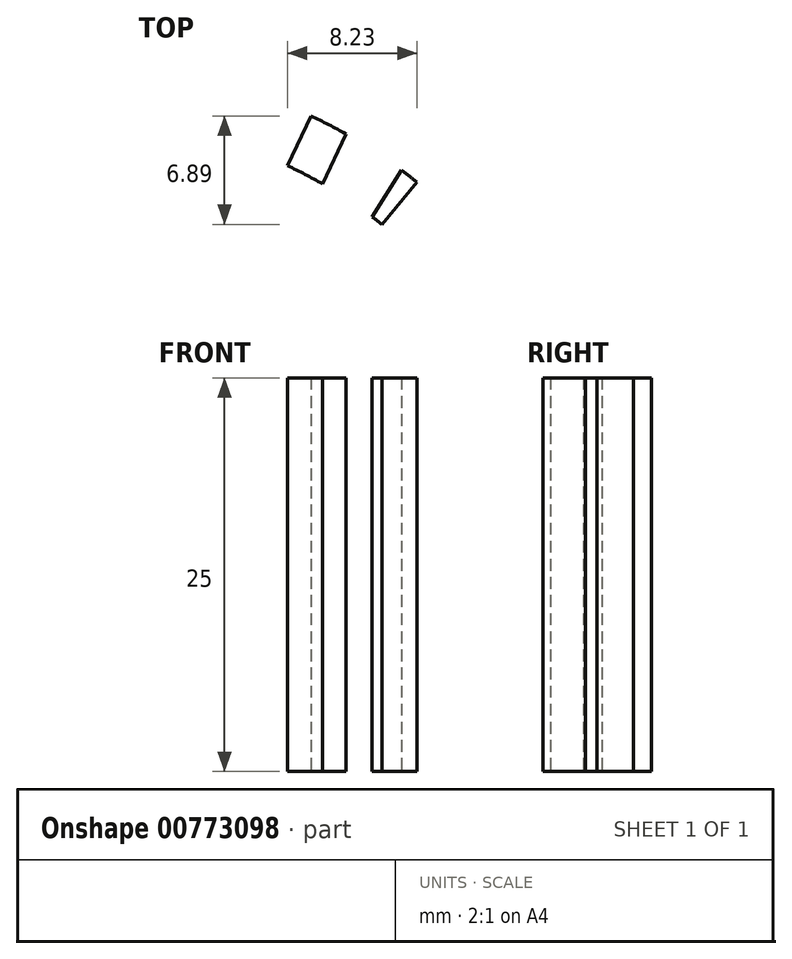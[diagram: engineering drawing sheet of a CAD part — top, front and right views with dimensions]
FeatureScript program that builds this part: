
annotation { "Feature Type Name" : "Feature", "Feature Type Description" : "" }
export const myFeature = defineFeature(function(context is Context, id is Id, definition is map)
    precondition{}
    {
        {
            var Q0;
            Q0=qCreatedBy(makeId("Top.planeOp"),FACE);
            var sketch = newSketch(context, id + "F0", { "sketchPlane" : qUnion([Q0])});
            skCircle(sketch, "E0", {"center": v(0, 0) * mm, "radius": 33.66 * mm});
            skCircle(sketch, "E1", {"center": v(0, 0) * mm, "radius": 30.16 * mm});
            skLineSegment(sketch, "E2", {"start": v(33.66, 0) * mm, "end": v(30.16, 0) * mm});
            skLineSegment(sketch, "E3", {"start": v(33.6, -2) * mm, "end": v(30.1, -2) * mm});
            skLineSegment(sketch, "E4", {"start": v(30.16, 0.5) * mm, "end": v(33.65, 0.5) * mm});
            skLineSegment(sketch, "E5", {"start": v(33.65, 0.5) * mm, "end": v(33.65, 0.5) * mm});
            skLineSegment(sketch, "E6", {"start": v(33.56, -2.5) * mm, "end": v(30.06, -2.5) * mm});
            skLineSegment(sketch, "E7.1.0", {"start": v(33.61, 1.73) * mm, "end": v(30.14, 1.29) * mm});
            skLineSegment(sketch, "E7.1.1", {"start": v(33.58, 2.23) * mm, "end": v(30.11, 1.79) * mm});
            skLineSegment(sketch, "E7.1.2", {"start": v(29.86, 4.28) * mm, "end": v(33.32, 4.71) * mm});
            skLineSegment(sketch, "E7.1.3", {"start": v(33.4, 4.22) * mm, "end": v(29.93, 3.78) * mm});
            skLineSegment(sketch, "E7.2.0", {"start": v(33.13, 5.93) * mm, "end": v(29.74, 5.06) * mm});
            skLineSegment(sketch, "E7.2.1", {"start": v(33.04, 6.42) * mm, "end": v(29.65, 5.55) * mm});
            skLineSegment(sketch, "E7.2.2", {"start": v(29.09, 7.98) * mm, "end": v(32.47, 8.85) * mm});
            skLineSegment(sketch, "E7.2.3", {"start": v(32.6, 8.37) * mm, "end": v(29.22, 7.5) * mm});
            skLineSegment(sketch, "E7.3.0", {"start": v(32.13, 10.03) * mm, "end": v(28.87, 8.74) * mm});
            skLineSegment(sketch, "E7.3.1", {"start": v(31.97, 10.5) * mm, "end": v(28.72, 9.22) * mm});
            skLineSegment(sketch, "E7.3.2", {"start": v(27.86, 11.57) * mm, "end": v(31.1, 12.85) * mm});
            skLineSegment(sketch, "E7.3.3", {"start": v(31.3, 12.39) * mm, "end": v(28.05, 11.1) * mm});
            skLineSegment(sketch, "E7.4.0", {"start": v(30.62, 13.98) * mm, "end": v(27.55, 12.3) * mm});
            skLineSegment(sketch, "E7.4.1", {"start": v(30.4, 14.43) * mm, "end": v(27.34, 12.75) * mm});
            skLineSegment(sketch, "E7.4.2", {"start": v(26.19, 14.97) * mm, "end": v(29.25, 16.65) * mm});
            skLineSegment(sketch, "E7.4.3", {"start": v(29.5, 16.21) * mm, "end": v(26.43, 14.53) * mm});
            skLineSegment(sketch, "E7.5.0", {"start": v(28.62, 17.7) * mm, "end": v(25.79, 15.65) * mm});
            skLineSegment(sketch, "E7.5.1", {"start": v(28.36, 18.13) * mm, "end": v(25.53, 16.07) * mm});
            skLineSegment(sketch, "E7.5.2", {"start": v(24.1, 18.13) * mm, "end": v(26.93, 20.18) * mm});
            skLineSegment(sketch, "E7.5.3", {"start": v(27.23, 19.78) * mm, "end": v(24.4, 17.73) * mm});
            skLineSegment(sketch, "E7.6.0", {"start": v(26.18, 21.15) * mm, "end": v(23.62, 18.76) * mm});
            skLineSegment(sketch, "E7.6.1", {"start": v(25.86, 21.54) * mm, "end": v(23.3, 19.15) * mm});
            skLineSegment(sketch, "E7.6.2", {"start": v(21.64, 21.01) * mm, "end": v(24.19, 23.4) * mm});
            skLineSegment(sketch, "E7.6.3", {"start": v(24.53, 23.04) * mm, "end": v(21.99, 20.65) * mm});
            skLineSegment(sketch, "E7.7.0", {"start": v(23.32, 24.27) * mm, "end": v(21.09, 21.57) * mm});
            skLineSegment(sketch, "E7.7.1", {"start": v(22.96, 24.61) * mm, "end": v(20.73, 21.92) * mm});
            skLineSegment(sketch, "E7.7.2", {"start": v(18.84, 23.56) * mm, "end": v(21.07, 26.25) * mm});
            skLineSegment(sketch, "E7.7.3", {"start": v(21.45, 25.93) * mm, "end": v(19.23, 23.24) * mm});
            skLineSegment(sketch, "E7.8.0", {"start": v(20.1, 27) * mm, "end": v(18.22, 24.04) * mm});
            skLineSegment(sketch, "E7.8.1", {"start": v(19.7, 27.3) * mm, "end": v(17.82, 24.34) * mm});
            skLineSegment(sketch, "E7.8.2", {"start": v(15.74, 25.73) * mm, "end": v(17.6, 28.68) * mm});
            skLineSegment(sketch, "E7.8.3", {"start": v(18.03, 28.42) * mm, "end": v(16.16, 25.47) * mm});
            skLineSegment(sketch, "E7.9.0", {"start": v(16.55, 29.3) * mm, "end": v(15.06, 26.14) * mm});
            skLineSegment(sketch, "E7.9.1", {"start": v(16.11, 29.55) * mm, "end": v(14.62, 26.38) * mm});
            skLineSegment(sketch, "E7.9.2", {"start": v(12.39, 27.5) * mm, "end": v(13.88, 30.66) * mm});
            skLineSegment(sketch, "E7.9.3", {"start": v(14.33, 30.45) * mm, "end": v(12.84, 27.3) * mm});
            skLineSegment(sketch, "E7.10.0", {"start": v(12.75, 31.15) * mm, "end": v(11.67, 27.82) * mm});
            skLineSegment(sketch, "E7.10.1", {"start": v(12.28, 31.33) * mm, "end": v(11.2, 28) * mm});
            skLineSegment(sketch, "E7.10.2", {"start": v(8.84, 28.84) * mm, "end": v(9.92, 32.16) * mm});
            skLineSegment(sketch, "E7.10.3", {"start": v(10.4, 32) * mm, "end": v(9.32, 28.69) * mm});
            skLineSegment(sketch, "E7.11.0", {"start": v(8.74, 32.5) * mm, "end": v(8.09, 29.06) * mm});
            skLineSegment(sketch, "E7.11.1", {"start": v(8.26, 32.63) * mm, "end": v(7.6, 29.19) * mm});
            skLineSegment(sketch, "E7.11.2", {"start": v(5.16, 29.72) * mm, "end": v(5.81, 33.15) * mm});
            skLineSegment(sketch, "E7.11.3", {"start": v(6.3, 33.06) * mm, "end": v(5.65, 29.63) * mm});
            skLineSegment(sketch, "E7.12.0", {"start": v(4.6, 33.34) * mm, "end": v(4.38, 29.84) * mm});
            skLineSegment(sketch, "E7.12.1", {"start": v(4.1, 33.4) * mm, "end": v(3.89, 29.91) * mm});
            skLineSegment(sketch, "E7.12.2", {"start": v(1.4, 30.13) * mm, "end": v(1.61, 33.62) * mm});
            skLineSegment(sketch, "E7.12.3", {"start": v(2.11, 33.59) * mm, "end": v(1.9, 30.1) * mm});
            skLineSegment(sketch, "E7.13.0", {"start": v(0.39, 33.65) * mm, "end": v(0.6, 30.16) * mm});
            skLineSegment(sketch, "E7.13.1", {"start": v(-0.11, 33.66) * mm, "end": v(0.1, 30.16) * mm});
            skLineSegment(sketch, "E7.13.2", {"start": v(-2.4, 30.07) * mm, "end": v(-2.61, 33.55) * mm});
            skLineSegment(sketch, "E7.13.3", {"start": v(-2.11, 33.59) * mm, "end": v(-1.9, 30.1) * mm});
            skLineSegment(sketch, "E7.14.0", {"start": v(-3.83, 33.44) * mm, "end": v(-3.18, 30) * mm});
            skLineSegment(sketch, "E7.14.1", {"start": v(-4.33, 33.38) * mm, "end": v(-3.68, 29.94) * mm});
            skLineSegment(sketch, "E7.14.2", {"start": v(-6.14, 29.53) * mm, "end": v(-6.8, 32.96) * mm});
            skLineSegment(sketch, "E7.14.3", {"start": v(-6.3, 33.06) * mm, "end": v(-5.65, 29.63) * mm});
            skLineSegment(sketch, "E7.15.0", {"start": v(-8, 32.7) * mm, "end": v(-6.91, 29.36) * mm});
            skLineSegment(sketch, "E7.15.1", {"start": v(-8.48, 32.57) * mm, "end": v(-7.4, 29.24) * mm});
            skLineSegment(sketch, "E7.15.2", {"start": v(-9.8, 28.53) * mm, "end": v(-10.87, 31.85) * mm});
            skLineSegment(sketch, "E7.15.3", {"start": v(-10.4, 32) * mm, "end": v(-9.32, 28.69) * mm});
            skLineSegment(sketch, "E7.16.0", {"start": v(-12.03, 31.43) * mm, "end": v(-10.54, 28.26) * mm});
            skLineSegment(sketch, "E7.16.1", {"start": v(-12.5, 31.25) * mm, "end": v(-11, 28.08) * mm});
            skLineSegment(sketch, "E7.16.2", {"start": v(-13.3, 27.08) * mm, "end": v(-14.78, 30.24) * mm});
            skLineSegment(sketch, "E7.16.3", {"start": v(-14.33, 30.45) * mm, "end": v(-12.84, 27.3) * mm});
            skLineSegment(sketch, "E7.17.0", {"start": v(-15.87, 29.68) * mm, "end": v(-14, 26.72) * mm});
            skLineSegment(sketch, "E7.17.1", {"start": v(-16.31, 29.44) * mm, "end": v(-14.44, 26.48) * mm});
            skLineSegment(sketch, "E7.17.2", {"start": v(-16.58, 25.2) * mm, "end": v(-18.45, 28.15) * mm});
            skLineSegment(sketch, "E7.17.3", {"start": v(-18.03, 28.42) * mm, "end": v(-16.16, 25.47) * mm});
            skLineSegment(sketch, "E7.18.0", {"start": v(-19.47, 27.45) * mm, "end": v(-17.24, 24.75) * mm});
            skLineSegment(sketch, "E7.18.1", {"start": v(-19.87, 27.16) * mm, "end": v(-17.64, 24.47) * mm});
            skLineSegment(sketch, "E7.18.2", {"start": v(-19.6, 22.92) * mm, "end": v(-21.84, 25.61) * mm});
            skLineSegment(sketch, "E7.18.3", {"start": v(-21.45, 25.93) * mm, "end": v(-19.23, 23.24) * mm});
            skLineSegment(sketch, "E7.19.0", {"start": v(-22.76, 24.8) * mm, "end": v(-20.2, 22.4) * mm});
            skLineSegment(sketch, "E7.19.1", {"start": v(-23.12, 24.46) * mm, "end": v(-20.57, 22.06) * mm});
            skLineSegment(sketch, "E7.19.2", {"start": v(-22.33, 20.28) * mm, "end": v(-24.87, 22.67) * mm});
            skLineSegment(sketch, "E7.19.3", {"start": v(-24.53, 23.04) * mm, "end": v(-21.99, 20.65) * mm});
            skLineSegment(sketch, "E7.20.0", {"start": v(-25.68, 21.75) * mm, "end": v(-22.85, 19.7) * mm});
            skLineSegment(sketch, "E7.20.1", {"start": v(-26, 21.37) * mm, "end": v(-23.17, 19.3) * mm});
            skLineSegment(sketch, "E7.20.2", {"start": v(-24.7, 17.32) * mm, "end": v(-27.52, 19.38) * mm});
            skLineSegment(sketch, "E7.20.3", {"start": v(-27.23, 19.78) * mm, "end": v(-24.4, 17.73) * mm});
            skLineSegment(sketch, "E7.21.0", {"start": v(-28.2, 18.36) * mm, "end": v(-25.14, 16.67) * mm});
            skLineSegment(sketch, "E7.21.1", {"start": v(-28.48, 17.94) * mm, "end": v(-25.41, 16.25) * mm});
            skLineSegment(sketch, "E7.21.2", {"start": v(-26.67, 14.1) * mm, "end": v(-29.73, 15.77) * mm});
            skLineSegment(sketch, "E7.21.3", {"start": v(-29.5, 16.21) * mm, "end": v(-26.43, 14.53) * mm});
            skLineSegment(sketch, "E7.22.0", {"start": v(-30.29, 14.68) * mm, "end": v(-27.03, 13.39) * mm});
            skLineSegment(sketch, "E7.22.1", {"start": v(-30.5, 14.23) * mm, "end": v(-27.25, 12.94) * mm});
            skLineSegment(sketch, "E7.22.2", {"start": v(-28.23, 10.64) * mm, "end": v(-31.47, 11.92) * mm});
            skLineSegment(sketch, "E7.22.3", {"start": v(-31.3, 12.39) * mm, "end": v(-28.05, 11.1) * mm});
            skLineSegment(sketch, "E7.23.0", {"start": v(-31.89, 10.77) * mm, "end": v(-28.5, 9.9) * mm});
            skLineSegment(sketch, "E7.23.1", {"start": v(-32.04, 10.3) * mm, "end": v(-28.65, 9.42) * mm});
            skLineSegment(sketch, "E7.23.2", {"start": v(-29.34, 7.02) * mm, "end": v(-32.72, 7.88) * mm});
            skLineSegment(sketch, "E7.23.3", {"start": v(-32.6, 8.37) * mm, "end": v(-29.22, 7.5) * mm});
            skLineSegment(sketch, "E7.24.0", {"start": v(-32.98, 6.69) * mm, "end": v(-29.51, 6.25) * mm});
            skLineSegment(sketch, "E7.24.1", {"start": v(-33.08, 6.2) * mm, "end": v(-29.6, 5.76) * mm});
            skLineSegment(sketch, "E7.24.2", {"start": v(-29.98, 3.28) * mm, "end": v(-33.45, 3.72) * mm});
            skLineSegment(sketch, "E7.24.3", {"start": v(-33.4, 4.22) * mm, "end": v(-29.93, 3.78) * mm});
            skLineSegment(sketch, "E7.25.0", {"start": v(-33.56, 2.5) * mm, "end": v(-30.06, 2.5) * mm});
            skLineSegment(sketch, "E7.25.1", {"start": v(-33.6, 2) * mm, "end": v(-30.1, 2) * mm});
            skLineSegment(sketch, "E7.25.2", {"start": v(-30.16, -0.5) * mm, "end": v(-33.65, -0.5) * mm});
            skLineSegment(sketch, "E7.25.3", {"start": v(-33.66, 0) * mm, "end": v(-30.16, 0) * mm});
            skLineSegment(sketch, "E7.26.0", {"start": v(-33.61, -1.73) * mm, "end": v(-30.14, -1.29) * mm});
            skLineSegment(sketch, "E7.26.1", {"start": v(-33.58, -2.23) * mm, "end": v(-30.11, -1.79) * mm});
            skLineSegment(sketch, "E7.26.2", {"start": v(-29.86, -4.28) * mm, "end": v(-33.32, -4.71) * mm});
            skLineSegment(sketch, "E7.26.3", {"start": v(-33.4, -4.22) * mm, "end": v(-29.93, -3.78) * mm});
            skLineSegment(sketch, "E7.27.0", {"start": v(-33.13, -5.93) * mm, "end": v(-29.74, -5.06) * mm});
            skLineSegment(sketch, "E7.27.1", {"start": v(-33.04, -6.42) * mm, "end": v(-29.65, -5.55) * mm});
            skLineSegment(sketch, "E7.27.2", {"start": v(-29.09, -7.98) * mm, "end": v(-32.47, -8.85) * mm});
            skLineSegment(sketch, "E7.27.3", {"start": v(-32.6, -8.37) * mm, "end": v(-29.22, -7.5) * mm});
            skLineSegment(sketch, "E7.28.0", {"start": v(-32.13, -10.03) * mm, "end": v(-28.87, -8.74) * mm});
            skLineSegment(sketch, "E7.28.1", {"start": v(-31.97, -10.5) * mm, "end": v(-28.72, -9.22) * mm});
            skLineSegment(sketch, "E7.28.2", {"start": v(-27.86, -11.57) * mm, "end": v(-31.1, -12.85) * mm});
            skLineSegment(sketch, "E7.28.3", {"start": v(-31.3, -12.39) * mm, "end": v(-28.05, -11.1) * mm});
            skLineSegment(sketch, "E7.29.0", {"start": v(-30.62, -13.98) * mm, "end": v(-27.55, -12.3) * mm});
            skLineSegment(sketch, "E7.29.1", {"start": v(-30.4, -14.43) * mm, "end": v(-27.34, -12.75) * mm});
            skLineSegment(sketch, "E7.29.2", {"start": v(-26.19, -14.97) * mm, "end": v(-29.25, -16.65) * mm});
            skLineSegment(sketch, "E7.29.3", {"start": v(-29.5, -16.21) * mm, "end": v(-26.43, -14.53) * mm});
            skLineSegment(sketch, "E7.30.0", {"start": v(-28.62, -17.7) * mm, "end": v(-25.79, -15.65) * mm});
            skLineSegment(sketch, "E7.30.1", {"start": v(-28.36, -18.13) * mm, "end": v(-25.53, -16.07) * mm});
            skLineSegment(sketch, "E7.30.2", {"start": v(-24.1, -18.13) * mm, "end": v(-26.93, -20.18) * mm});
            skLineSegment(sketch, "E7.30.3", {"start": v(-27.23, -19.78) * mm, "end": v(-24.4, -17.73) * mm});
            skLineSegment(sketch, "E7.31.0", {"start": v(-26.18, -21.15) * mm, "end": v(-23.62, -18.76) * mm});
            skLineSegment(sketch, "E7.31.1", {"start": v(-25.86, -21.54) * mm, "end": v(-23.3, -19.15) * mm});
            skLineSegment(sketch, "E7.31.2", {"start": v(-21.64, -21.01) * mm, "end": v(-24.19, -23.4) * mm});
            skLineSegment(sketch, "E7.31.3", {"start": v(-24.53, -23.04) * mm, "end": v(-21.99, -20.65) * mm});
            skLineSegment(sketch, "E7.32.0", {"start": v(-23.32, -24.27) * mm, "end": v(-21.09, -21.57) * mm});
            skLineSegment(sketch, "E7.32.1", {"start": v(-22.96, -24.61) * mm, "end": v(-20.73, -21.92) * mm});
            skLineSegment(sketch, "E7.32.2", {"start": v(-18.84, -23.56) * mm, "end": v(-21.07, -26.25) * mm});
            skLineSegment(sketch, "E7.32.3", {"start": v(-21.45, -25.93) * mm, "end": v(-19.23, -23.24) * mm});
            skLineSegment(sketch, "E7.33.0", {"start": v(-20.1, -27) * mm, "end": v(-18.22, -24.04) * mm});
            skLineSegment(sketch, "E7.33.1", {"start": v(-19.7, -27.3) * mm, "end": v(-17.82, -24.34) * mm});
            skLineSegment(sketch, "E7.33.2", {"start": v(-15.74, -25.73) * mm, "end": v(-17.6, -28.68) * mm});
            skLineSegment(sketch, "E7.33.3", {"start": v(-18.03, -28.42) * mm, "end": v(-16.16, -25.47) * mm});
            skLineSegment(sketch, "E7.34.0", {"start": v(-16.55, -29.3) * mm, "end": v(-15.06, -26.14) * mm});
            skLineSegment(sketch, "E7.34.1", {"start": v(-16.11, -29.55) * mm, "end": v(-14.62, -26.38) * mm});
            skLineSegment(sketch, "E7.34.2", {"start": v(-12.39, -27.5) * mm, "end": v(-13.88, -30.66) * mm});
            skLineSegment(sketch, "E7.34.3", {"start": v(-14.33, -30.45) * mm, "end": v(-12.84, -27.3) * mm});
            skLineSegment(sketch, "E7.35.0", {"start": v(-12.75, -31.15) * mm, "end": v(-11.67, -27.82) * mm});
            skLineSegment(sketch, "E7.35.1", {"start": v(-12.28, -31.33) * mm, "end": v(-11.2, -28) * mm});
            skLineSegment(sketch, "E7.35.2", {"start": v(-8.84, -28.84) * mm, "end": v(-9.92, -32.16) * mm});
            skLineSegment(sketch, "E7.35.3", {"start": v(-10.4, -32) * mm, "end": v(-9.32, -28.69) * mm});
            skLineSegment(sketch, "E7.36.0", {"start": v(-8.74, -32.5) * mm, "end": v(-8.09, -29.06) * mm});
            skLineSegment(sketch, "E7.36.1", {"start": v(-8.26, -32.63) * mm, "end": v(-7.6, -29.19) * mm});
            skLineSegment(sketch, "E7.36.2", {"start": v(-5.16, -29.72) * mm, "end": v(-5.81, -33.15) * mm});
            skLineSegment(sketch, "E7.36.3", {"start": v(-6.3, -33.06) * mm, "end": v(-5.65, -29.63) * mm});
            skLineSegment(sketch, "E7.37.0", {"start": v(-4.6, -33.34) * mm, "end": v(-4.38, -29.84) * mm});
            skLineSegment(sketch, "E7.37.1", {"start": v(-4.1, -33.4) * mm, "end": v(-3.89, -29.91) * mm});
            skLineSegment(sketch, "E7.37.2", {"start": v(-1.4, -30.13) * mm, "end": v(-1.61, -33.62) * mm});
            skLineSegment(sketch, "E7.37.3", {"start": v(-2.11, -33.59) * mm, "end": v(-1.9, -30.1) * mm});
            skLineSegment(sketch, "E7.38.0", {"start": v(-0.39, -33.65) * mm, "end": v(-0.6, -30.16) * mm});
            skLineSegment(sketch, "E7.38.1", {"start": v(0.11, -33.66) * mm, "end": v(-0.1, -30.16) * mm});
            skLineSegment(sketch, "E7.38.2", {"start": v(2.4, -30.07) * mm, "end": v(2.61, -33.55) * mm});
            skLineSegment(sketch, "E7.38.3", {"start": v(2.11, -33.59) * mm, "end": v(1.9, -30.1) * mm});
            skLineSegment(sketch, "E7.39.0", {"start": v(3.83, -33.44) * mm, "end": v(3.18, -30) * mm});
            skLineSegment(sketch, "E7.39.1", {"start": v(4.33, -33.38) * mm, "end": v(3.68, -29.94) * mm});
            skLineSegment(sketch, "E7.39.2", {"start": v(6.14, -29.53) * mm, "end": v(6.8, -32.96) * mm});
            skLineSegment(sketch, "E7.39.3", {"start": v(6.3, -33.06) * mm, "end": v(5.65, -29.63) * mm});
            skLineSegment(sketch, "E7.40.0", {"start": v(8, -32.7) * mm, "end": v(6.91, -29.36) * mm});
            skLineSegment(sketch, "E7.40.1", {"start": v(8.48, -32.57) * mm, "end": v(7.4, -29.24) * mm});
            skLineSegment(sketch, "E7.40.2", {"start": v(9.8, -28.53) * mm, "end": v(10.87, -31.85) * mm});
            skLineSegment(sketch, "E7.40.3", {"start": v(10.4, -32) * mm, "end": v(9.32, -28.69) * mm});
            skLineSegment(sketch, "E7.41.0", {"start": v(12.03, -31.43) * mm, "end": v(10.54, -28.26) * mm});
            skLineSegment(sketch, "E7.41.1", {"start": v(12.5, -31.25) * mm, "end": v(11, -28.08) * mm});
            skLineSegment(sketch, "E7.41.2", {"start": v(13.3, -27.08) * mm, "end": v(14.78, -30.24) * mm});
            skLineSegment(sketch, "E7.41.3", {"start": v(14.33, -30.45) * mm, "end": v(12.84, -27.3) * mm});
            skLineSegment(sketch, "E7.42.0", {"start": v(15.87, -29.68) * mm, "end": v(14, -26.72) * mm});
            skLineSegment(sketch, "E7.42.1", {"start": v(16.31, -29.44) * mm, "end": v(14.44, -26.48) * mm});
            skLineSegment(sketch, "E7.42.2", {"start": v(16.58, -25.2) * mm, "end": v(18.45, -28.15) * mm});
            skLineSegment(sketch, "E7.42.3", {"start": v(18.03, -28.42) * mm, "end": v(16.16, -25.47) * mm});
            skLineSegment(sketch, "E7.43.0", {"start": v(19.47, -27.45) * mm, "end": v(17.24, -24.75) * mm});
            skLineSegment(sketch, "E7.43.1", {"start": v(19.87, -27.16) * mm, "end": v(17.64, -24.47) * mm});
            skLineSegment(sketch, "E7.43.2", {"start": v(19.6, -22.92) * mm, "end": v(21.84, -25.61) * mm});
            skLineSegment(sketch, "E7.43.3", {"start": v(21.45, -25.93) * mm, "end": v(19.23, -23.24) * mm});
            skLineSegment(sketch, "E7.44.0", {"start": v(22.76, -24.8) * mm, "end": v(20.2, -22.4) * mm});
            skLineSegment(sketch, "E7.44.1", {"start": v(23.12, -24.46) * mm, "end": v(20.57, -22.06) * mm});
            skLineSegment(sketch, "E7.44.2", {"start": v(22.33, -20.28) * mm, "end": v(24.87, -22.67) * mm});
            skLineSegment(sketch, "E7.44.3", {"start": v(24.53, -23.04) * mm, "end": v(21.99, -20.65) * mm});
            skLineSegment(sketch, "E7.45.0", {"start": v(25.68, -21.75) * mm, "end": v(22.85, -19.7) * mm});
            skLineSegment(sketch, "E7.45.1", {"start": v(26, -21.37) * mm, "end": v(23.17, -19.3) * mm});
            skLineSegment(sketch, "E7.45.2", {"start": v(24.7, -17.32) * mm, "end": v(27.52, -19.38) * mm});
            skLineSegment(sketch, "E7.45.3", {"start": v(27.23, -19.78) * mm, "end": v(24.4, -17.73) * mm});
            skLineSegment(sketch, "E7.46.0", {"start": v(28.2, -18.36) * mm, "end": v(25.14, -16.67) * mm});
            skLineSegment(sketch, "E7.46.1", {"start": v(28.48, -17.94) * mm, "end": v(25.41, -16.25) * mm});
            skLineSegment(sketch, "E7.46.2", {"start": v(26.67, -14.1) * mm, "end": v(29.73, -15.77) * mm});
            skLineSegment(sketch, "E7.46.3", {"start": v(29.5, -16.21) * mm, "end": v(26.43, -14.53) * mm});
            skLineSegment(sketch, "E7.47.0", {"start": v(30.29, -14.68) * mm, "end": v(27.03, -13.39) * mm});
            skLineSegment(sketch, "E7.47.1", {"start": v(30.5, -14.23) * mm, "end": v(27.25, -12.94) * mm});
            skLineSegment(sketch, "E7.47.2", {"start": v(28.23, -10.64) * mm, "end": v(31.47, -11.92) * mm});
            skLineSegment(sketch, "E7.47.3", {"start": v(31.3, -12.39) * mm, "end": v(28.05, -11.1) * mm});
            skLineSegment(sketch, "E7.48.0", {"start": v(31.89, -10.77) * mm, "end": v(28.5, -9.9) * mm});
            skLineSegment(sketch, "E7.48.1", {"start": v(32.04, -10.3) * mm, "end": v(28.65, -9.42) * mm});
            skLineSegment(sketch, "E7.48.2", {"start": v(29.34, -7.02) * mm, "end": v(32.72, -7.88) * mm});
            skLineSegment(sketch, "E7.48.3", {"start": v(32.6, -8.37) * mm, "end": v(29.22, -7.5) * mm});
            skLineSegment(sketch, "E7.49.0", {"start": v(32.98, -6.69) * mm, "end": v(29.51, -6.25) * mm});
            skLineSegment(sketch, "E7.49.1", {"start": v(33.08, -6.2) * mm, "end": v(29.6, -5.76) * mm});
            skLineSegment(sketch, "E7.49.2", {"start": v(29.98, -3.28) * mm, "end": v(33.45, -3.72) * mm});
            skLineSegment(sketch, "E7.49.3", {"start": v(33.4, -4.22) * mm, "end": v(29.93, -3.78) * mm});
            skSolve(sketch);
        }
        {
            var Q0;
            {var subQ0=sQuery(id+"F0.wireOp",EDGE,"E7.7.2");Q0=makeQuery(id+"F0.imprint","IMPRINT",FACE,{"disambiguationData":[TD([[makeQuery(id+"F0.imprint","IMPRINT",EDGE,{"derivedFrom":subQ0}),1.0]])]});}
            var Q1;
            {var subQ0=sQuery(id+"F0.wireOp",EDGE,"E7.9.0");Q1=makeQuery(id+"F0.imprint","IMPRINT",FACE,{"disambiguationData":[TD([[makeQuery(id+"F0.imprint","IMPRINT",EDGE,{"derivedFrom":subQ0}),-1.0]])]});}
            var Q2;
            {var subQ0=sQuery(id+"F0.wireOp",EDGE,"E7.9.1");Q2=makeQuery(id+"F0.imprint","IMPRINT",FACE,{"disambiguationData":[TD([[makeQuery(id+"F0.imprint","IMPRINT",EDGE,{"derivedFrom":subQ0}),-1.0]])]});}
            extrude(context, id + "F1", {"entities" : qUnion([Q0, Q1, Q2]), "depth" : 25 * mm, "offsetDistance" : 25 * mm});
        }
    });
